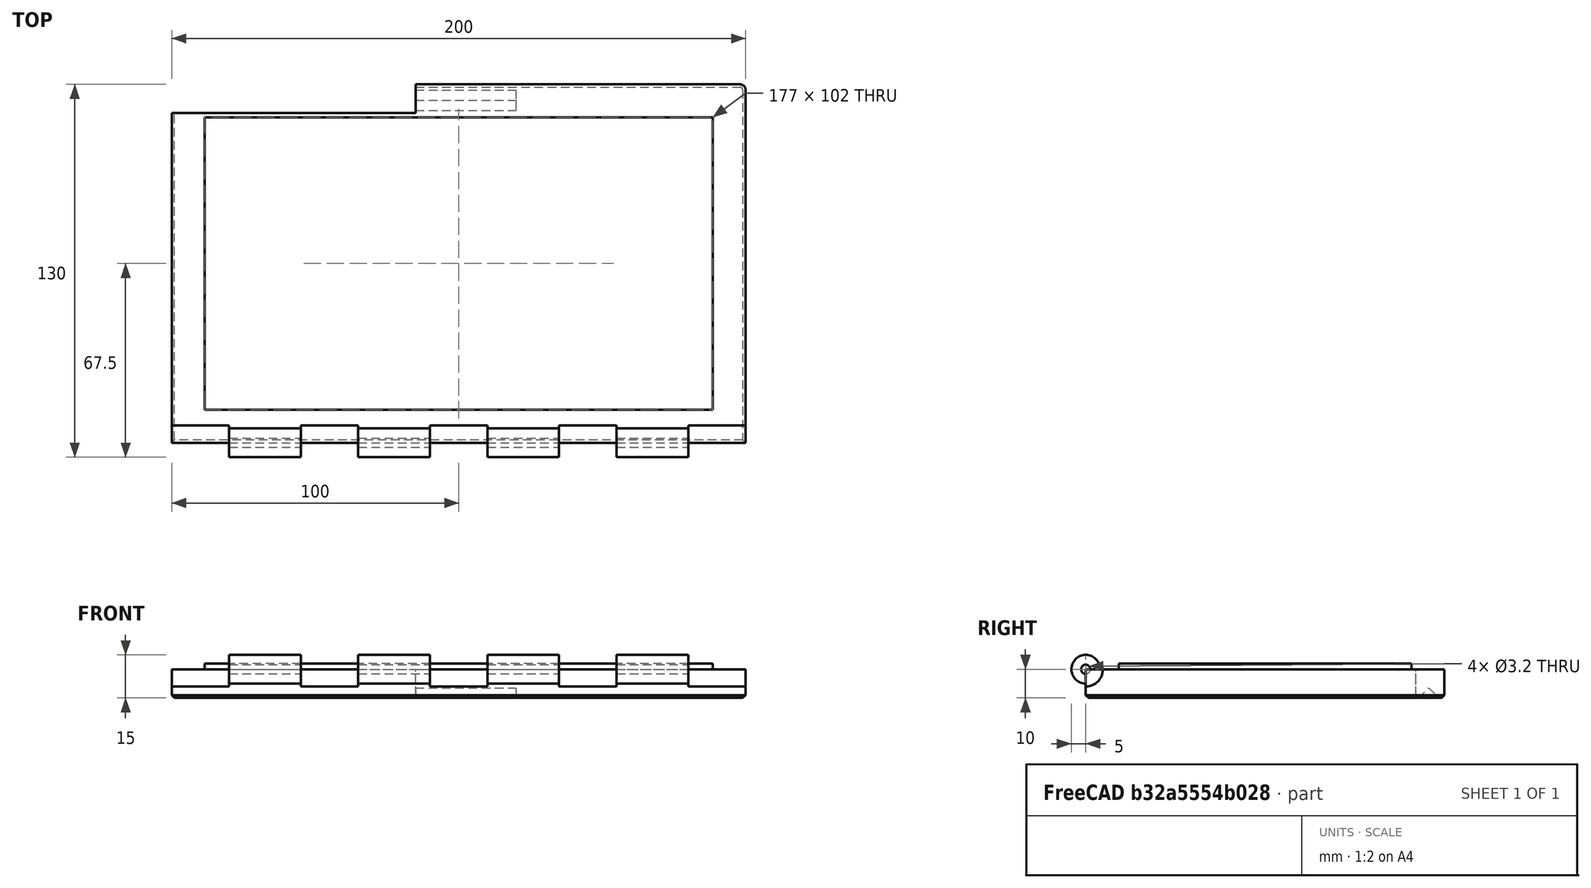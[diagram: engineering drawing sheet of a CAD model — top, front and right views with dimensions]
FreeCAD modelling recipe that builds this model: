
FCSTD DOCUMENT  (FreeCAD 0.19R)
Label: SwichCaseSmallSkirt
License: All rights reserved
LicenseURL: http://en.wikipedia.org/wiki/All_rights_reserved
objects: Part::Cylinder×10, Sketcher::SketchObject×4, Part::MultiFuse×3, PartDesign::Chamfer×3, PartDesign::Pad×2, PartDesign::Pocket×2, Part::Cut×2, PartDesign::ShapeBinder×1, PartDesign::Fillet×1, PartDesign::Body×1, Mesh::Feature×1
note: 37 computed .brp shape members not serialized (recipe doc carries the construction recipe); baked Part::Feature solids carry a one-line shape summary decoded from their .brp

FEATURE [Sketcher::SketchObject] Sketch
  FullyConstrained = true
  MapMode = 5
  Support = -> [XY_Plane]
  sketch-geometry (4):
    g0: LineSegment StartX=-100 StartY=62.5 StartZ=0 EndX=100 EndY=62.5 EndZ=0
    g1: LineSegment StartX=100 StartY=62.5 StartZ=0 EndX=100 EndY=-62.5 EndZ=0
    g2: LineSegment StartX=100 StartY=-62.5 StartZ=0 EndX=-100 EndY=-62.5 EndZ=0
    g3: LineSegment StartX=-100 StartY=-62.5 StartZ=0 EndX=-100 EndY=62.5 EndZ=0
  constraints (11):
    c: Coincident(g0,g1)
    c: Coincident(g1,g2)
    c: Coincident(g2,g3)
    c: Coincident(g3,g0)
    c: Horizontal(g0)
    c: Horizontal(g2)
    c: Vertical(g1)
    c: Vertical(g3)
    c: Symmetric(g0,g2,g-1)
    c: Distance(g0) = 200
    c: Distance(g1) = 125
FEATURE [PartDesign::Pad] Pad
  Direction = (1,1,1)
  Length = 10
  Length2 = 100
  Profile = -> Sketch
  Type = 0
FEATURE [Sketcher::SketchObject] Sketch001
  FullyConstrained = true
  MapMode = 5
  Placement = pos=(0,0,10) rot=(0,0,1;0rad)
  Support = -> [Pad]
  sketch-geometry (4):
    g0: LineSegment StartX=-88.5 StartY=51 StartZ=0 EndX=88.5 EndY=51 EndZ=0
    g1: LineSegment StartX=88.5 StartY=51 StartZ=0 EndX=88.5 EndY=-51 EndZ=0
    g2: LineSegment StartX=88.5 StartY=-51 StartZ=0 EndX=-88.5 EndY=-51 EndZ=0
    g3: LineSegment StartX=-88.5 StartY=-51 StartZ=0 EndX=-88.5 EndY=51 EndZ=0
  constraints (11):
    c: Coincident(g0,g1)
    c: Coincident(g1,g2)
    c: Coincident(g2,g3)
    c: Coincident(g3,g0)
    c: Horizontal(g0)
    c: Horizontal(g2)
    c: Vertical(g1)
    c: Vertical(g3)
    c: Distance(g0) = 177
    c: Distance(g1) = 102
    c: Symmetric(g0,g2,g-1)
FEATURE [PartDesign::Pad] Pad001
  BaseFeature = -> Pad
  Direction = (1,1,1)
  Length = 2
  Length2 = 100
  Profile = -> Sketch001
  Type = 0
FEATURE [Part::Cylinder] Cylinder
  Angle = 360
  AttacherType = Attacher::AttachEngine3D
  Height = 25
  Placement = pos=(55,-62.5,10) rot=(0,1,0;1.5708rad)
  Radius = 5
FEATURE [Part::Cylinder] Cylinder001
  Angle = 360
  AttacherType = Attacher::AttachEngine3D
  Height = 25
  Placement = pos=(10,-62.5,10) rot=(0,1,0;1.5708rad)
  Radius = 5
FEATURE [Part::Cylinder] Cylinder002
  Angle = 360
  AttacherType = Attacher::AttachEngine3D
  Height = 25
  Placement = pos=(-35,-62.5,10) rot=(0,1,0;1.5708rad)
  Radius = 5
FEATURE [Part::Cylinder] Cylinder003
  Angle = 360
  AttacherType = Attacher::AttachEngine3D
  Height = 25
  Placement = pos=(-80,-62.5,10) rot=(0,1,0;1.5708rad)
  Radius = 5
FEATURE [Part::Cylinder] Cylinder004 .. Cylinder008  x5 (patterned run collapsed; names and placements below)
  Angle = 360
  AttacherType = Attacher::AttachEngine3D
  Height = 20
  Radius = 6
  placements: 5 in arithmetic series — first pos=(80,-62.5,10) rot=(0,1,0;1.5708rad), step (-45,0,0), last pos=(-100,-62.5,10) rot=(0,1,0;1.5708rad)
FEATURE [Part::Cylinder] Cylinder009
  Angle = 360
  AttacherType = Attacher::AttachEngine3D
  Height = 220
  Placement = pos=(-110,-62.5,10) rot=(0,1,0;1.5708rad)
  Radius = 1.6
FEATURE [PartDesign::ShapeBinder] CopyCut001
  TraceSupport = false
FEATURE [Sketcher::SketchObject] Sketch002
  ExternalGeometry = -> [Pad001]
  FullyConstrained = true
  MapMode = 5
  Placement = pos=(-100,0,0) rot=(0.57735,-0.57735,-0.57735;2.0944rad)
  Support = -> [Pad001]
  sketch-geometry (4):
    g0: LineSegment StartX=-60.5 StartY=0 StartZ=0 EndX=-56.9645 EndY=3.53553 EndZ=0
    g1: LineSegment StartX=-56.9645 StartY=3.53553 StartZ=0 EndX=-53.4289 EndY=-1.4011e-12 EndZ=0
    g2: LineSegment StartX=-53.4289 StartY=-1.4011e-12 StartZ=0 EndX=-56.9645 EndY=-3.53553 EndZ=0
    g3: LineSegment StartX=-56.9645 StartY=-3.53553 StartZ=0 EndX=-60.5 EndY=0 EndZ=0
  constraints (12):
    c: Coincident(g0,g1)
    c: Coincident(g1,g2)
    c: Coincident(g2,g3)
    c: Coincident(g3,g0)
    c: Equal(g2,g3)
    c: Equal(g3,g0)
    c: Equal(g0,g1)
    c: Perpendicular(g1,g0)
    c: Angle(g1) = -0.785398
    c: Distance(g1) = 5
    c: PointOnObject(g0,g-1)
    c: Distance(g0,g-3) = 2
FEATURE [PartDesign::Pocket] Pocket
  BaseFeature = -> Pad001
  Length = 120
  Length2 = 100
  Profile = -> Sketch002
  Type = 0
FEATURE [Part::MultiFuse] Fusion
  Shapes = -> [Cylinder,Cylinder001,Cylinder002,Cylinder003]
FEATURE [Part::MultiFuse] Fusion001
  Shapes = -> [Cylinder004,Cylinder005,Cylinder006,Cylinder007,Cylinder008]
FEATURE [Sketcher::SketchObject] Sketch003
  ExternalGeometry = -> [Pocket]
  FullyConstrained = true
  MapMode = 5
  Placement = pos=(0,0,0) rot=(1,0,0;3.14159rad)
  Support = -> [Pocket]
  sketch-geometry (4):
    g0: LineSegment StartX=-15 StartY=-62.5 StartZ=0 EndX=-100 EndY=-62.5 EndZ=0
    g1: LineSegment StartX=-100 StartY=-62.5 StartZ=0 EndX=-100 EndY=-52.5 EndZ=0
    g2: LineSegment StartX=-100 StartY=-52.5 StartZ=0 EndX=-15 EndY=-52.5 EndZ=0
    g3: LineSegment StartX=-15 StartY=-52.5 StartZ=0 EndX=-15 EndY=-62.5 EndZ=0
  constraints (11):
    c: Coincident(g0,g1)
    c: Coincident(g1,g2)
    c: Coincident(g2,g3)
    c: Coincident(g3,g0)
    c: Horizontal(g0)
    c: Horizontal(g2)
    c: Vertical(g1)
    c: Vertical(g3)
    c: Distance(g1) = 10
    c: Coincident(g0,g-3)
    c: DistanceX(g0) = -15
FEATURE [PartDesign::Pocket] Pocket001
  BaseFeature = -> Pocket
  Length = 5
  Length2 = 100
  Profile = -> Sketch003
  Type = 1
FEATURE [PartDesign::Fillet] Fillet
  Base = -> Pocket001 [Edge2]
  BaseFeature = -> Pocket001
  Radius = 2
  SupportTransform = false
FEATURE [PartDesign::Chamfer] Chamfer
  Angle = 45
  Base = -> Fillet [Edge5]
  BaseFeature = -> Fillet
  ChamferType = 0
  FlipDirection = false
  Size = 1
  Size2 = 1
  SupportTransform = false
FEATURE [PartDesign::Chamfer] Chamfer001
  Angle = 45
  Base = -> Chamfer [Edge31]
  BaseFeature = -> Chamfer
  ChamferType = 0
  FlipDirection = false
  Size = 1
  Size2 = 1
  SupportTransform = false
FEATURE [PartDesign::Chamfer] Chamfer002
  Angle = 45
  Base = -> Chamfer001 [Edge1]
  BaseFeature = -> Chamfer001
  ChamferType = 0
  FlipDirection = false
  Size = 1
  Size2 = 1
  SupportTransform = false
FEATURE [PartDesign::Body] Body
  Group = -> [Sketch,Pad,Sketch001,Pad001,CopyCut001,Sketch002,Pocket,Sketch003,Pocket001,Fillet,Chamfer,Chamfer001,Chamfer002]
  Origin = -> Origin
  Tip = -> Chamfer002
FEATURE [Part::MultiFuse] Fusion002
  Shapes = -> [Fusion,Chamfer002]
FEATURE [Part::Cut] Cut
  Base = -> Fusion002
  Tool = -> Fusion001
FEATURE [Part::Cut] Cut001
  Base = -> Cut
  Tool = -> Cylinder009
FEATURE [Mesh::Feature] Mesh  label="Cut001 (Meshed)"
